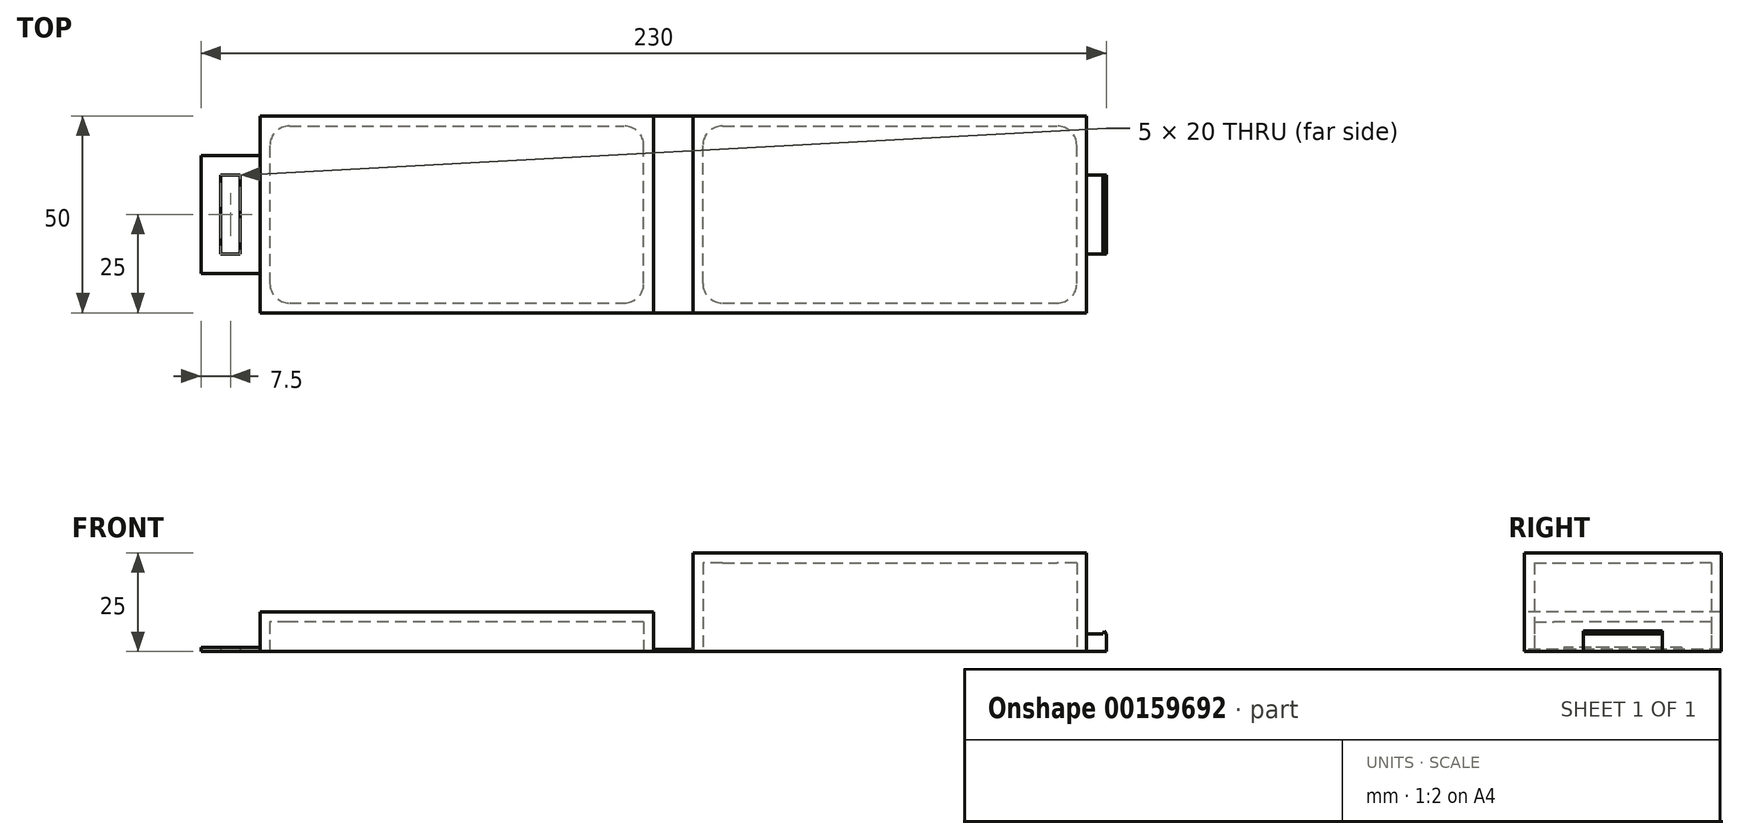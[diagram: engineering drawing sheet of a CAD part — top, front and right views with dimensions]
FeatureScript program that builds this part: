
annotation { "Feature Type Name" : "Feature", "Feature Type Description" : "" }
export const myFeature = defineFeature(function(context is Context, id is Id, definition is map)
    precondition{}
    {
        {
            var Q0;
            Q0=qCreatedBy(makeId("Top.planeOp"),FACE);
            var sketch = newSketch(context, id + "F0", { "sketchPlane" : qUnion([Q0])});
            skLineSegment(sketch, "E0.bottom", {"start": v(-50, -25) * mm, "end": v(50, -25) * mm});
            skLineSegment(sketch, "E0.top", {"start": v(-50, 25) * mm, "end": v(50, 25) * mm});
            skLineSegment(sketch, "E0.left", {"start": v(-50, -25) * mm, "end": v(-50, 25) * mm});
            skLineSegment(sketch, "E0.right", {"start": v(50, -25) * mm, "end": v(50, 25) * mm});
            skPoint(sketch, "E0.middle", {"position": v(0, 0) * mm});
            skSolve(sketch);
        }
        {
            var Q0;
            Q0 = qSketchRegion(id + "F0", true);
            extrude(context, id + "F1", {"entities" : qUnion([Q0]), "depth" : 25 * mm});
        }
        {
            var Q0;
            Q0=qCreatedBy(makeId("Top.planeOp"),FACE);
            var sketch = newSketch(context, id + "F2", { "sketchPlane" : qUnion([Q0])});
            skPoint(sketch, "E1.0", {"position": v(-50, 25) * mm});
            skPoint(sketch, "E1.1", {"position": v(-50, -25) * mm});
            skLineSegment(sketch, "E2.bottom", {"start": v(-50, 25) * mm, "end": v(-60, 25) * mm});
            skLineSegment(sketch, "E2.top", {"start": v(-50, -25) * mm, "end": v(-60, -25) * mm});
            skLineSegment(sketch, "E2.left", {"start": v(-50, 25) * mm, "end": v(-50, -25) * mm});
            skLineSegment(sketch, "E2.right", {"start": v(-60, 25) * mm, "end": v(-60, -25) * mm});
            skSolve(sketch);
        }
        {
            var Q0;
            Q0=makeQuery(id+"F2.imprint","IMPRINT",FACE,{"disambiguationData":[TD([[makeQuery(id+"F2.imprint","IMPRINT",EDGE,{"derivedFrom":sQuery(id+"F2.wireOp",EDGE,"E2.bottom")}),1.0]])]});
            extrude(context, id + "F3", {"entities" : qUnion([Q0]), "operationType" : NewBodyOperationType.ADD, "depth" : .5 * mm});
        }
        {
            var Q0;
            Q0=qCreatedBy(makeId("Top.planeOp"),FACE);
            var sketch = newSketch(context, id + "F4", { "sketchPlane" : qUnion([Q0])});
            skPoint(sketch, "E3.0", {"position": v(-60, 25) * mm});
            skPoint(sketch, "E3.1", {"position": v(-60, -25) * mm});
            skLineSegment(sketch, "E4.bottom", {"start": v(-60, 25) * mm, "end": v(-160, 25) * mm});
            skLineSegment(sketch, "E4.top", {"start": v(-60, -25) * mm, "end": v(-160, -25) * mm});
            skLineSegment(sketch, "E4.left", {"start": v(-60, 25) * mm, "end": v(-60, -25) * mm});
            skLineSegment(sketch, "E4.right", {"start": v(-160, 25) * mm, "end": v(-160, -25) * mm});
            skSolve(sketch);
        }
        {
            var Q0;
            Q0 = qSketchRegion(id + "F4", true);
            extrude(context, id + "F5", {"entities" : qUnion([Q0]), "operationType" : NewBodyOperationType.ADD, "depth" : 10 * mm});
        }
        {
            var Q0;
            Q0=makeQuery(id+"F5.boolean.opBoolean","MERGE",FACE,{"derivedFrom":[makeQuery(id+"F3.boolean.opBoolean","MERGE",FACE,{"derivedFrom":[makeQuery(id+"F1.opExtrude","CAP_FACE",FACE,{"disambiguationData":[OSD([sQuery(id+"F0.wireOp",EDGE,"E0.bottom"),sQuery(id+"F0.wireOp",EDGE,"E0.top"),sQuery(id+"F0.wireOp",EDGE,"E0.left"),sQuery(id+"F0.wireOp",EDGE,"E0.right")])],"isStart":true}),makeQuery(id+"F3.opExtrude","CAP_FACE",FACE,{"disambiguationData":[OSD([sQuery(id+"F2.wireOp",EDGE,"E2.bottom"),sQuery(id+"F2.wireOp",EDGE,"E2.top"),sQuery(id+"F2.wireOp",EDGE,"E2.left"),sQuery(id+"F2.wireOp",EDGE,"E2.right")])],"isStart":true})]}),makeQuery(id+"F5.opExtrude","CAP_FACE",FACE,{"disambiguationData":[OSD([sQuery(id+"F4.wireOp",EDGE,"E4.bottom"),sQuery(id+"F4.wireOp",EDGE,"E4.top"),sQuery(id+"F4.wireOp",EDGE,"E4.left"),sQuery(id+"F4.wireOp",EDGE,"E4.right")])],"isStart":true})]});
            shell(context, id + "F6", {"entities" : qUnion([Q0]), "thickness" : 2.5 * mm});
        }
        {
            var Q0;
            Q0=makeQuery(id+"F6.opShell","OFFSET_EDGE",EDGE,{"disambiguationData":[OSD([sQuery(id+"F4.wireOp",EDGE,"E4.top"),sQuery(id+"F4.wireOp",EDGE,"E4.right")])]});
            var Q1;
            Q1=makeQuery(id+"F6.opShell","OFFSET_EDGE",EDGE,{"disambiguationData":[OSD([sQuery(id+"F4.wireOp",EDGE,"E4.top"),sQuery(id+"F4.wireOp",EDGE,"E4.left")])]});
            var Q2;
            Q2=makeQuery(id+"F6.opShell","OFFSET_EDGE",EDGE,{"disambiguationData":[OSD([sQuery(id+"F4.wireOp",EDGE,"E4.bottom"),sQuery(id+"F4.wireOp",EDGE,"E4.left")])]});
            var Q3;
            Q3=makeQuery(id+"F6.opShell","OFFSET_EDGE",EDGE,{"disambiguationData":[OSD([sQuery(id+"F4.wireOp",EDGE,"E4.bottom"),sQuery(id+"F4.wireOp",EDGE,"E4.right")])]});
            var Q4;
            Q4=makeQuery(id+"F6.opShell","OFFSET_EDGE",EDGE,{"disambiguationData":[OSD([sQuery(id+"F0.wireOp",EDGE,"E0.bottom"),sQuery(id+"F0.wireOp",EDGE,"E0.left")])]});
            var Q5;
            Q5=makeQuery(id+"F6.opShell","OFFSET_EDGE",EDGE,{"disambiguationData":[OSD([sQuery(id+"F0.wireOp",EDGE,"E0.bottom"),sQuery(id+"F0.wireOp",EDGE,"E0.right")])]});
            var Q6;
            Q6=makeQuery(id+"F6.opShell","OFFSET_EDGE",EDGE,{"disambiguationData":[OSD([sQuery(id+"F0.wireOp",EDGE,"E0.top"),sQuery(id+"F0.wireOp",EDGE,"E0.right")])]});
            var Q7;
            Q7=makeQuery(id+"F6.opShell","OFFSET_EDGE",EDGE,{"disambiguationData":[OSD([sQuery(id+"F0.wireOp",EDGE,"E0.top"),sQuery(id+"F0.wireOp",EDGE,"E0.left")])]});
            fillet(context, id + "F7", {"entities" : qUnion([Q0, Q1, Q2, Q3, Q4, Q5, Q6, Q7]), "radius" : 5 * mm, "tangentPropagation" : true, "allowEdgeOverflow" : false});
        }
        {
            var Q0;
            Q0=qCreatedBy(makeId("Top.planeOp"),FACE);
            var sketch = newSketch(context, id + "F8", { "sketchPlane" : qUnion([Q0])});
            skLineSegment(sketch, "E5.bottom", {"start": v(50, 10) * mm, "end": v(55, 10) * mm});
            skLineSegment(sketch, "E5.top", {"start": v(50, -10) * mm, "end": v(55, -10) * mm});
            skLineSegment(sketch, "E5.left", {"start": v(50, 10) * mm, "end": v(50, -10) * mm});
            skLineSegment(sketch, "E5.right", {"start": v(55, 10) * mm, "end": v(55, -10) * mm});
            skLineSegment(sketch, "E6", {"start": v(0, 0) * mm, "end": v(104.12, 0) * mm, "construction": true});
            skSolve(sketch);
        }
        {
            var Q0;
            Q0 = qSketchRegion(id + "F8", true);
            extrude(context, id + "F9", {"entities" : qUnion([Q0]), "operationType" : NewBodyOperationType.ADD, "depth" : 4.5 * mm});
        }
        {
            var Q0;
            Q0=qCreatedBy(makeId("Top.planeOp"),FACE);
            var sketch = newSketch(context, id + "F10", { "sketchPlane" : qUnion([Q0])});
            skLineSegment(sketch, "E7.bottom", {"start": v(-160, 15) * mm, "end": v(-175, 15) * mm});
            skLineSegment(sketch, "E7.top", {"start": v(-160, -15) * mm, "end": v(-175, -15) * mm});
            skLineSegment(sketch, "E7.left", {"start": v(-160, 15) * mm, "end": v(-160, -15) * mm});
            skLineSegment(sketch, "E7.right", {"start": v(-175, 15) * mm, "end": v(-175, -15) * mm});
            skLineSegment(sketch, "E8", {"start": v(0, 0) * mm, "end": v(-202.15, 0) * mm, "construction": true});
            skLineSegment(sketch, "E9.bottom", {"start": v(-170, 10) * mm, "end": v(-165, 10) * mm});
            skLineSegment(sketch, "E9.top", {"start": v(-170, -10) * mm, "end": v(-165, -10) * mm});
            skLineSegment(sketch, "E9.left", {"start": v(-170, 10) * mm, "end": v(-170, -10) * mm});
            skLineSegment(sketch, "E9.right", {"start": v(-165, 10) * mm, "end": v(-165, -10) * mm});
            skPoint(sketch, "E9.middle", {"position": v(-167.5, 0) * mm});
            skLineSegment(sketch, "E10", {"start": v(-167.5, 15) * mm, "end": v(-167.5, -21.24) * mm, "construction": true});
            skSolve(sketch);
        }
        {
            var Q0;
            Q0 = qSketchRegion(id + "F10", true);
            extrude(context, id + "F11", {"entities" : qUnion([Q0]), "operationType" : NewBodyOperationType.ADD, "depth" : 1 * mm});
        }
        {
            var Q0;
            Q0=qCreatedBy(makeId("Front.planeOp"),FACE);
            var sketch = newSketch(context, id + "F12", { "sketchPlane" : qUnion([Q0])});
            skCircle(sketch, "E11.cCircle", {"center": v(54.57, 4.75) * mm, "radius": 0.5 * mm, "construction": true});
            skLineSegment(sketch, "E11.0", {"start": v(54.57, 5.25) * mm, "end": v(55, 4.5) * mm});
            skLineSegment(sketch, "E11.1", {"start": v(55, 4.5) * mm, "end": v(54.13, 4.5) * mm});
            skLineSegment(sketch, "E11.2", {"start": v(54.13, 4.5) * mm, "end": v(54.57, 5.25) * mm});
            skSolve(sketch);
        }
        {
            var Q0;
            Q0 = qSketchRegion(id + "F12", true);
            extrude(context, id + "F13", {"entities" : qUnion([Q0]), "operationType" : NewBodyOperationType.ADD, "endBound" : BoundingType.SYMMETRIC, "depth" : 20 * mm});
        }
    });
